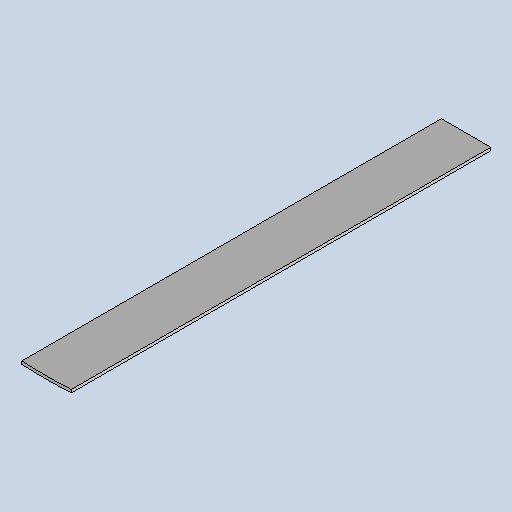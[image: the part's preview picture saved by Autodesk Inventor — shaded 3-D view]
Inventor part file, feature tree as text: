
AUTODESK INVENTOR PART (.ipt)
format: ipt  version: 2025 (Build 290162010, 162A)  size: 254,976 bytes
history: native  units: mm
features: sheet_metal_op x1, sketch x1, other x1
ambient origin geometry x8: Origin, YZ Plane, XZ Plane, XY Plane, X Axis, Y Axis, Z Axis, Center Point
bodies: Body1 (feature_tree)
feature tree (3):
  sheet_metal_op  "Face2"
  sketch  "Sketch1"  dims[d11=1100.0mm d12=900.0mm d13=25.0mm d14=25.0mm d15=3.0mm d16=25.0mm]
  other  "Plate2"
